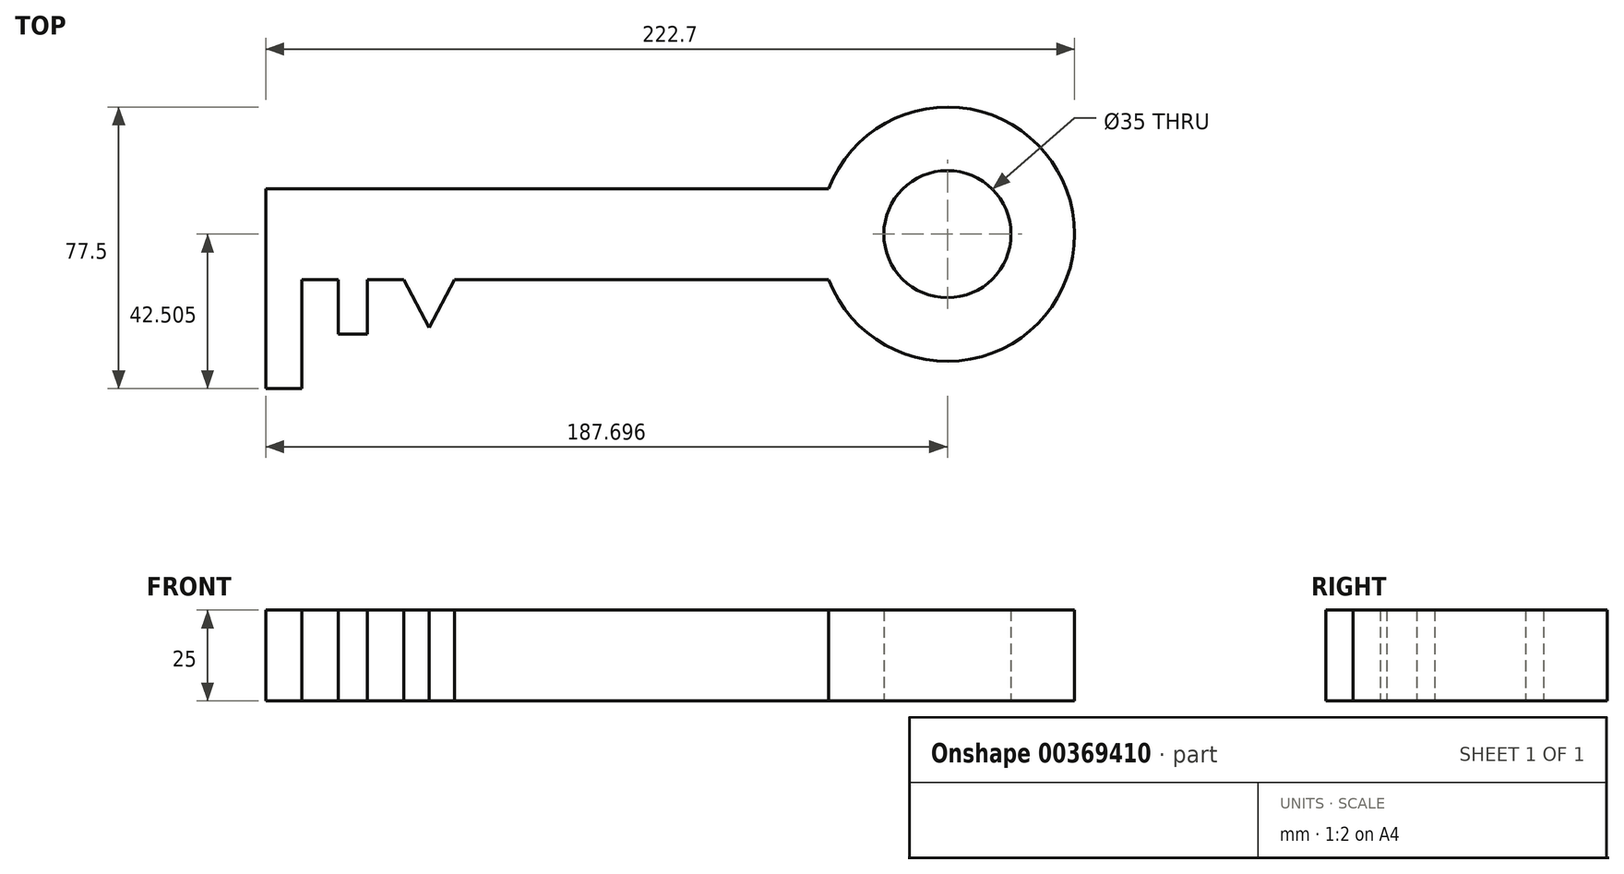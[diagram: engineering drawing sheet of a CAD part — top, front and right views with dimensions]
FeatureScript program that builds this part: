
annotation { "Feature Type Name" : "Feature", "Feature Type Description" : "" }
export const myFeature = defineFeature(function(context is Context, id is Id, definition is map)
    precondition{}
    {
        {
            var Q0;
            Q0=qCreatedBy(makeId("Top.planeOp"),FACE);
            var sketch = newSketch(context, id + "F0", { "sketchPlane" : qUnion([Q0])});
            skLineSegment(sketch, "E0.bottom", {"start": v(-90.09, 37.96) * mm, "end": v(64.91, 37.96) * mm});
            skLineSegment(sketch, "E0.top", {"start": v(-90.09, 12.96) * mm, "end": v(64.91, 12.96) * mm});
            skLineSegment(sketch, "E0.left", {"start": v(-90.09, 37.96) * mm, "end": v(-90.09, 12.96) * mm});
            skLineSegment(sketch, "E1.bottom", {"start": v(-90.09, 12.96) * mm, "end": v(-80.09, 12.96) * mm});
            skLineSegment(sketch, "E1.top", {"start": v(-90.09, -17.04) * mm, "end": v(-80.09, -17.04) * mm});
            skLineSegment(sketch, "E1.left", {"start": v(-90.09, 12.96) * mm, "end": v(-90.09, -17.04) * mm});
            skLineSegment(sketch, "E1.right", {"start": v(-80.09, 12.96) * mm, "end": v(-80.09, -17.04) * mm});
            skLineSegment(sketch, "E2.bottom", {"start": v(-70.09, 12.96) * mm, "end": v(-62.09, 12.96) * mm});
            skLineSegment(sketch, "E2.top", {"start": v(-70.09, -2.04) * mm, "end": v(-62.09, -2.04) * mm});
            skLineSegment(sketch, "E2.left", {"start": v(-70.09, 12.96) * mm, "end": v(-70.09, -2.04) * mm});
            skLineSegment(sketch, "E2.right", {"start": v(-62.09, 12.96) * mm, "end": v(-62.09, -2.04) * mm});
            skLineSegment(sketch, "E3", {"start": v(-52.09, 12.96) * mm, "end": v(-45.09, -0.3) * mm});
            skLineSegment(sketch, "E4", {"start": v(-45.09, -0.3) * mm, "end": v(-38.09, 12.96) * mm});
            skLineSegment(sketch, "E5", {"start": v(-38.09, 12.96) * mm, "end": v(-52.09, 12.96) * mm});
            skArc(sketch, "E6", {"start": v(64.91, 12.96) * mm, "mid": v(132.6, 25.46) * mm, "end": v(64.91, 37.96) * mm});
            skCircle(sketch, "E7", {"center": v(97.6, 25.46) * mm, "radius": 17.5 * mm});
            skSolve(sketch);
        }
        {
            var Q0;
            Q0 = qSketchRegion(id + "F0", true);
            extrude(context, id + "F1", {"entities" : qUnion([Q0]), "depth" : 25 * mm});
        }
    });
